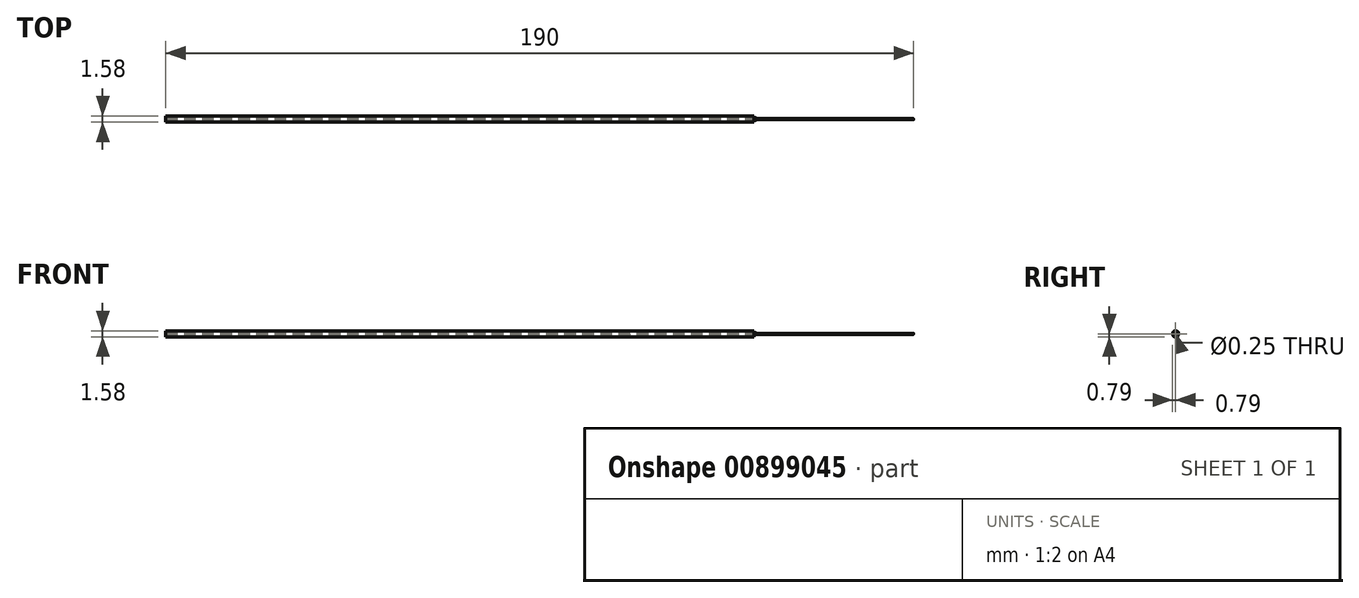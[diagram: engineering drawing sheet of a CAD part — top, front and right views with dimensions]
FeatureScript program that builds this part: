
annotation { "Feature Type Name" : "Feature", "Feature Type Description" : "" }
export const myFeature = defineFeature(function(context is Context, id is Id, definition is map)
    precondition{}
    {
        {
            var Q0;
            Q0=qCreatedBy(makeId("Right.planeOp"),FACE);
            var sketch = newSketch(context, id + "F0", { "sketchPlane" : qUnion([Q0])});
            skCircle(sketch, "E0", {"center": v(0, 0) * mm, "radius": 0.13 * mm});
            skSolve(sketch);
        }
        {
            var Q0;
            Q0 = qSketchRegion(id + "F0", true);
            extrude(context, id + "F1", {"entities" : qUnion([Q0]), "endBound" : BoundingType.SYMMETRIC, "depth" : 40 * mm, "offsetDistance" : 25.4 * mm});
        }
        {
            var Q0;
            Q0=makeQuery(id+"F1.opExtrude","CAP_FACE",FACE,{"disambiguationData":[OSD([sQuery(id+"F0.wireOp",EDGE,"E0")])],"isStart":true});
            var sketch = newSketch(context, id + "F2", { "sketchPlane" : qUnion([Q0])});
            skCircle(sketch, "E1.0.0", {"center": v(0, 0) * mm, "radius": 0.13 * mm});
            skCircle(sketch, "E2", {"center": v(0, 0) * mm, "radius": 0.79 * mm});
            skSolve(sketch);
        }
        {
            var Q0;
            Q0 = qSketchRegion(id + "F2", true);
            extrude(context, id + "F3", {"entities" : qUnion([Q0]), "depth" : 150 * mm, "offsetDistance" : 25.4 * mm});
        }
        {
            var Q0;
            Q0=makeQuery(id+"F3.opExtrude","CAP_EDGE",EDGE,{"disambiguationData":[OSD([sQuery(id+"F2.wireOp",EDGE,"E2")])],"isStart":true});
            fillet(context, id + "F4", {"entities" : qUnion([Q0]), "radius" : 0.5 * mm, "tangentPropagation" : true, "allowEdgeOverflow" : false});
        }
    });
